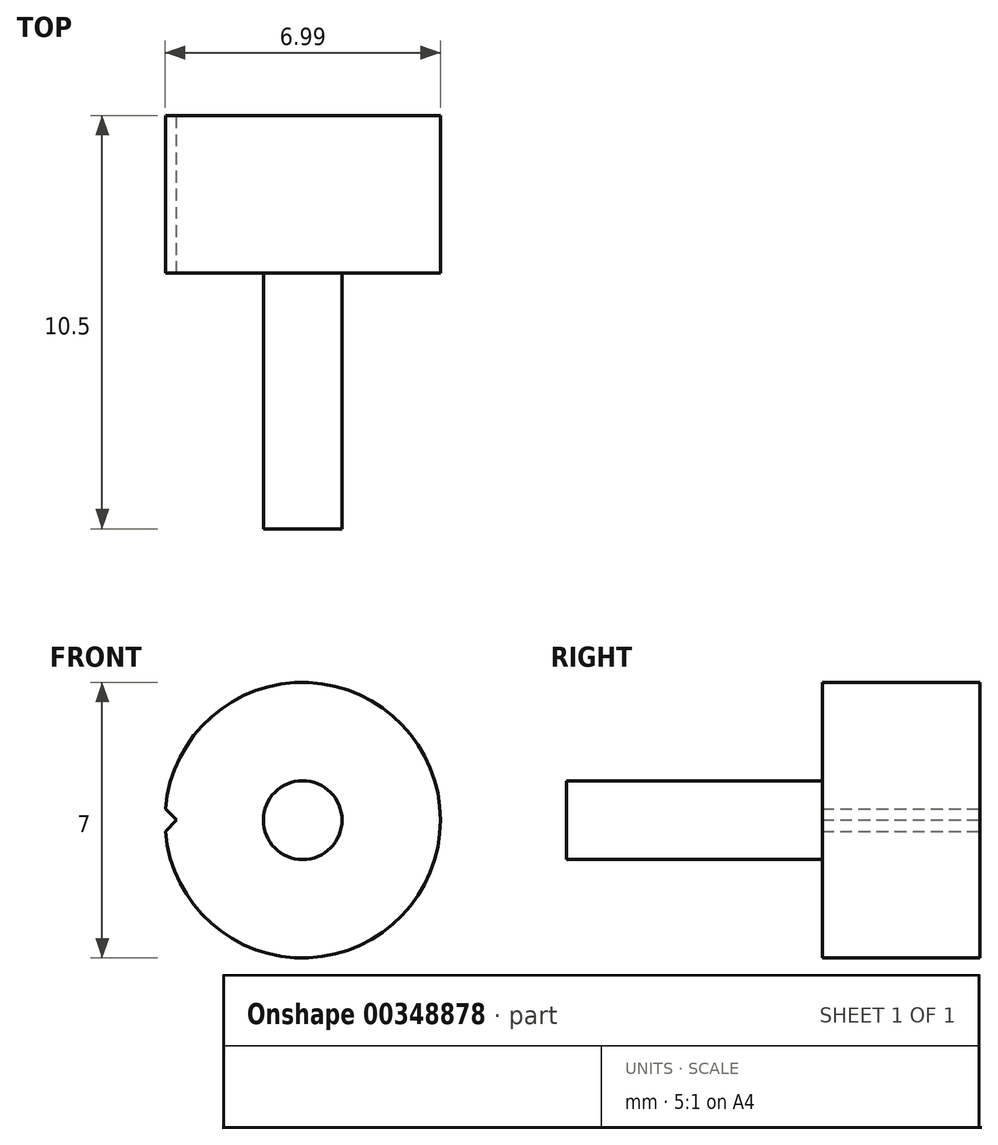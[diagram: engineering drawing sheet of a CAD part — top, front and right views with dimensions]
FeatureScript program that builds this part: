
annotation { "Feature Type Name" : "Feature", "Feature Type Description" : "" }
export const myFeature = defineFeature(function(context is Context, id is Id, definition is map)
    precondition{}
    {
        {
            var Q0;
            Q0=qCreatedBy(makeId("Front.planeOp"),FACE);
            var sketch = newSketch(context, id + "F0", { "sketchPlane" : qUnion([Q0])});
            skCircle(sketch, "E0", {"center": v(0, 0) * mm, "radius": 1 * mm});
            skSolve(sketch);
        }
        {
            var Q0;
            Q0=qSketchRegion(id+"F0",true);
            extrude(context, id + "F1", {"entities" : qUnion([Q0]), "depth" : 6.5 * mm});
        }
        {
            var Q0;
            Q0=makeQuery(id+"F1.opExtrude","CAP_FACE",FACE,{"disambiguationData":[OSD([sQuery(id+"F0.wireOp",EDGE,"E0")])],"isStart":true});
            var sketch = newSketch(context, id + "F2", { "sketchPlane" : qUnion([Q0])});
            skCircle(sketch, "E1", {"center": v(0, 0) * mm, "radius": 3.5 * mm});
            skSolve(sketch);
        }
        {
            var Q0;
            Q0=qSketchRegion(id+"F2",true);
            extrude(context, id + "F3", {"entities" : qUnion([Q0]), "operationType" : NewBodyOperationType.ADD, "depth" : 4 * mm});
        }
        {
            var Q0;
            Q0=makeQuery(id+"F3.opExtrude","CAP_FACE",FACE,{"disambiguationData":[OSD([sQuery(id+"F2.wireOp",EDGE,"E1")])],"isStart":false});
            var sketch = newSketch(context, id + "F4", { "sketchPlane" : qUnion([Q0])});
            skArc(sketch, "E2.0", {"start": v(3.49, -0.29) * mm, "mid": v(3.5, 0) * mm, "end": v(3.49, 0.29) * mm});
            skLineSegment(sketch, "E3", {"start": v(-0.15, 0) * mm, "end": v(3.5, 0) * mm, "construction": true});
            skLineSegment(sketch, "E4", {"start": v(3.49, -0.29) * mm, "end": v(3.2, 0) * mm});
            skLineSegment(sketch, "E5", {"start": v(3.2, 0) * mm, "end": v(3.49, 0.29) * mm});
            skSolve(sketch);
        }
        {
            var Q0;
            Q0=qSketchRegion(id+"F4",true);
            extrude(context, id + "F5", {"entities" : qUnion([Q0]), "operationType" : NewBodyOperationType.REMOVE, "endBound" : BoundingType.THROUGH_ALL, "oppositeDirection" : true, "depth" : 25 * mm});
        }
    });
